# Revit family: RN 62010 Vanne à glissière
name_source: partatom
category: Rohrzubehör
units: mm (PartAtom-declared; Revit-internal decimal feet)

## family parameters
Arbeitsebenenbasiert = Nein
Beim Laden mit Abzugskörper schneiden = Nein
Bemaßung runder Anschluss = Durchmesser verwenden
Gemeinsam genutzt = Nein
Immer vertikal = Ja
Teiletyp = Ventil - Zerlegung in

## types (10) — shared parameters
1.010.00.2 Blattnummer der Richtlinie = 17
1.010.00.3 Ausgabedatum (Monat) der Richtlinie = 201601
1.010.00.4 Herstellername = R. Nussbaum AG
1.010.00.5 Revisionsdatum der Datei = 20190528
1.010.00.6 Webadresse des Herstellers = http://www.nussbaum.ch
1.100.00.3 Sortiernummer für Anzeigereihenfolge = 1
1.100.00.4 Produktbezeichnung = Absperrarmaturen
1.960/3L.00.8 Link (URL) = https://www.nussbaum.ch
17.700.00.4 Armaturentyp = 1
17.700.00.7 Maximale Betriebstemperatur TB [°C] = 40
17.700.00.8 Maximaler Betriebsdruck (Arbeitsdruck) ps [1.0 · 105 Pa] = 16
Connector Visibility = Nein
EnclosingSpace Visibility = Nein
Hersteller = R. Nussbauzm AG
URL = https://www.nussbaum.ch

## per-type parameters (varying)
- DN 25: 1.800.00.3 TGA-Nummer=00102100000000000000000000000400600000000000000001???00000; 1.810.00.3 Hersteller-Bestellnummer=62010.23; 1.810.00.4 DATANORM-Nummer=62010.23; 1.810.00.5 StLB-Nummer=721.153; 1.810.00.6 GTIN-Nummer=7612945672926; 17.700.00.30 Produktbeschreibung=62010.23, Schieber, mit Flanschen, DN=25; 17.700.00.5 Nennweite DN=25; 17.700.00.6 kvs-Wert [m3/h]=20.6; CONNECTOR0_DIAMETER_dX_0r=25 mm  [stored 0.082021 ft]; CONNECTOR0_dX_00=66 mm; CONNECTOR0_dX_01=65 mm; CONNECTOR0_ref_dX=66 mm; CONNECTOR1_DIAMETER_dX_0r=25 mm  [stored 0.082021 ft]; CONNECTOR1_dX_00=65 mm; CONNECTOR1_dX_01=66 mm; CONNECTOR1_ref_dX=66 mm; Modell=62010.23; R. Nussbaum AG 62010.23 de Visibility=Ja; R. Nussbaum AG 62010.24 de Visibility=Nein; R. Nussbaum AG 62010.25 de Visibility=Nein; R. Nussbaum AG 62010.26 de Visibility=Nein; R. Nussbaum AG 62010.27 de Visibility=Nein; R. Nussbaum AG 62010.28 de Visibility=Nein; R. Nussbaum AG 62010.29 de Visibility=Nein; R. Nussbaum AG 62010.30 de Visibility=Nein; R. Nussbaum AG 62010.31 de Visibility=Nein; R. Nussbaum AG 62010.32 de Visibility=Nein; Typenkommentare=Vanne à glissièreDN 25
- DN 32: 1.800.00.3 TGA-Nummer=00102100000000000000000000000400600000000000000002???00000; 1.810.00.3 Hersteller-Bestellnummer=62010.24; 1.810.00.4 DATANORM-Nummer=62010.24; 1.810.00.5 StLB-Nummer=721.154; 1.810.00.6 GTIN-Nummer=7612945672933; 17.700.00.30 Produktbeschreibung=62010.24, Schieber, mit Flanschen, DN=32; 17.700.00.5 Nennweite DN=32; 17.700.00.6 kvs-Wert [m3/h]=36.8; CONNECTOR0_DIAMETER_dX_0r=32 mm; CONNECTOR0_dX_00=71 mm; CONNECTOR0_dX_01=70 mm; CONNECTOR0_ref_dX=71 mm; CONNECTOR1_DIAMETER_dX_0r=32 mm; CONNECTOR1_dX_00=70 mm; CONNECTOR1_dX_01=71 mm; CONNECTOR1_ref_dX=71 mm; Modell=62010.24; R. Nussbaum AG 62010.23 de Visibility=Nein; R. Nussbaum AG 62010.24 de Visibility=Ja; R. Nussbaum AG 62010.25 de Visibility=Nein; R. Nussbaum AG 62010.26 de Visibility=Nein; R. Nussbaum AG 62010.27 de Visibility=Nein; R. Nussbaum AG 62010.28 de Visibility=Nein; R. Nussbaum AG 62010.29 de Visibility=Nein; R. Nussbaum AG 62010.30 de Visibility=Nein; R. Nussbaum AG 62010.31 de Visibility=Nein; R. Nussbaum AG 62010.32 de Visibility=Nein; Typenkommentare=Vanne à glissièreDN 32
- DN 40: 1.800.00.3 TGA-Nummer=00102100000000000000000000000400600000000000000003???00000; 1.810.00.3 Hersteller-Bestellnummer=62010.25; 1.810.00.4 DATANORM-Nummer=62010.25; 1.810.00.5 StLB-Nummer=721.155; 1.810.00.6 GTIN-Nummer=7612945016492; 17.700.00.30 Produktbeschreibung=62010.25, Schieber, mit Flanschen, DN=40; 17.700.00.5 Nennweite DN=40; 17.700.00.6 kvs-Wert [m3/h]=45.2; CONNECTOR0_DIAMETER_dX_0r=40 mm; CONNECTOR0_dX_00=71 mm; CONNECTOR0_dX_01=70 mm; CONNECTOR0_ref_dX=71 mm; CONNECTOR1_DIAMETER_dX_0r=40 mm; CONNECTOR1_dX_00=70 mm; CONNECTOR1_dX_01=71 mm; CONNECTOR1_ref_dX=71 mm; Modell=62010.25; R. Nussbaum AG 62010.23 de Visibility=Nein; R. Nussbaum AG 62010.24 de Visibility=Nein; R. Nussbaum AG 62010.25 de Visibility=Ja; R. Nussbaum AG 62010.26 de Visibility=Nein; R. Nussbaum AG 62010.27 de Visibility=Nein; R. Nussbaum AG 62010.28 de Visibility=Nein; R. Nussbaum AG 62010.29 de Visibility=Nein; R. Nussbaum AG 62010.30 de Visibility=Nein; R. Nussbaum AG 62010.31 de Visibility=Nein; R. Nussbaum AG 62010.32 de Visibility=Nein; Typenkommentare=Vanne à glissièreDN 40
- DN 50: 1.800.00.3 TGA-Nummer=00102100000000000000000000000400600000000000000004???00000; 1.810.00.3 Hersteller-Bestellnummer=62010.26; 1.810.00.4 DATANORM-Nummer=62010.26; 1.810.00.5 StLB-Nummer=721.156; 1.810.00.6 GTIN-Nummer=7612945016508; 17.700.00.30 Produktbeschreibung=62010.26, Schieber, mit Flanschen, DN=50; 17.700.00.5 Nennweite DN=50; 17.700.00.6 kvs-Wert [m3/h]=76.1; CONNECTOR0_DIAMETER_dX_0r=50 mm  [stored 0.164042 ft]; CONNECTOR0_dX_00=76 mm; CONNECTOR0_dX_01=75 mm; CONNECTOR0_ref_dX=76 mm; CONNECTOR1_DIAMETER_dX_0r=50 mm  [stored 0.164042 ft]; CONNECTOR1_dX_00=75 mm; CONNECTOR1_dX_01=76 mm; CONNECTOR1_ref_dX=76 mm; Modell=62010.26; R. Nussbaum AG 62010.23 de Visibility=Nein; R. Nussbaum AG 62010.24 de Visibility=Nein; R. Nussbaum AG 62010.25 de Visibility=Nein; R. Nussbaum AG 62010.26 de Visibility=Ja; R. Nussbaum AG 62010.27 de Visibility=Nein; R. Nussbaum AG 62010.28 de Visibility=Nein; R. Nussbaum AG 62010.29 de Visibility=Nein; R. Nussbaum AG 62010.30 de Visibility=Nein; R. Nussbaum AG 62010.31 de Visibility=Nein; R. Nussbaum AG 62010.32 de Visibility=Nein; Typenkommentare=Vanne à glissièreDN 50
- DN 65: 1.800.00.3 TGA-Nummer=00102100000000000000000000000400600000000000000005???00000; 1.810.00.3 Hersteller-Bestellnummer=62010.27; 1.810.00.4 DATANORM-Nummer=62010.27; 1.810.00.5 StLB-Nummer=721.157; 1.810.00.6 GTIN-Nummer=7612945016515; 17.700.00.30 Produktbeschreibung=62010.27, Schieber, mit Flanschen, DN=65; 17.700.00.5 Nennweite DN=65; 17.700.00.6 kvs-Wert [m3/h]=115.5; CONNECTOR0_DIAMETER_dX_0r=65 mm; CONNECTOR0_dX_00=86 mm; CONNECTOR0_dX_01=85 mm; CONNECTOR0_ref_dX=86 mm; CONNECTOR1_DIAMETER_dX_0r=65 mm; CONNECTOR1_dX_00=85 mm; CONNECTOR1_dX_01=86 mm; CONNECTOR1_ref_dX=86 mm; Modell=62010.27; R. Nussbaum AG 62010.23 de Visibility=Nein; R. Nussbaum AG 62010.24 de Visibility=Nein; R. Nussbaum AG 62010.25 de Visibility=Nein; R. Nussbaum AG 62010.26 de Visibility=Nein; R. Nussbaum AG 62010.27 de Visibility=Ja; R. Nussbaum AG 62010.28 de Visibility=Nein; R. Nussbaum AG 62010.29 de Visibility=Nein; R. Nussbaum AG 62010.30 de Visibility=Nein; R. Nussbaum AG 62010.31 de Visibility=Nein; R. Nussbaum AG 62010.32 de Visibility=Nein; Typenkommentare=Vanne à glissièreDN 65
- DN 80: 1.800.00.3 TGA-Nummer=00102100000000000000000000000400600000000000000006???00000; 1.810.00.3 Hersteller-Bestellnummer=62010.28; 1.810.00.4 DATANORM-Nummer=62010.28; 1.810.00.5 StLB-Nummer=721.158; 1.810.00.6 GTIN-Nummer=7612945016522; 17.700.00.30 Produktbeschreibung=62010.28, Schieber, mit Flanschen, DN=80; 17.700.00.5 Nennweite DN=80; 17.700.00.6 kvs-Wert [m3/h]=158.4; CONNECTOR0_DIAMETER_dX_0r=80 mm; CONNECTOR0_dX_00=91 mm; CONNECTOR0_dX_01=90 mm; CONNECTOR0_ref_dX=91 mm; CONNECTOR1_DIAMETER_dX_0r=80 mm; CONNECTOR1_dX_00=90 mm; CONNECTOR1_dX_01=91 mm; CONNECTOR1_ref_dX=91 mm; Modell=62010.28; R. Nussbaum AG 62010.23 de Visibility=Nein; R. Nussbaum AG 62010.24 de Visibility=Nein; R. Nussbaum AG 62010.25 de Visibility=Nein; R. Nussbaum AG 62010.26 de Visibility=Nein; R. Nussbaum AG 62010.27 de Visibility=Nein; R. Nussbaum AG 62010.28 de Visibility=Ja; R. Nussbaum AG 62010.29 de Visibility=Nein; R. Nussbaum AG 62010.30 de Visibility=Nein; R. Nussbaum AG 62010.31 de Visibility=Nein; R. Nussbaum AG 62010.32 de Visibility=Nein; Typenkommentare=Vanne à glissièreDN 80
- DN 100: 1.800.00.3 TGA-Nummer=00102100000000000000000000000400600000000000000007???00000; 1.810.00.3 Hersteller-Bestellnummer=62010.29; 1.810.00.4 DATANORM-Nummer=62010.29; 1.810.00.5 StLB-Nummer=721.161; 1.810.00.6 GTIN-Nummer=7612945016539; 17.700.00.30 Produktbeschreibung=62010.29, Schieber, mit Flanschen, DN=100; 17.700.00.5 Nennweite DN=100; 17.700.00.6 kvs-Wert [m3/h]=233; CONNECTOR0_DIAMETER_dX_0r=100 mm  [stored 0.328084 ft]; CONNECTOR0_dX_00=96 mm; CONNECTOR0_dX_01=95 mm; CONNECTOR0_ref_dX=96 mm; CONNECTOR1_DIAMETER_dX_0r=100 mm  [stored 0.328084 ft]; CONNECTOR1_dX_00=95 mm; CONNECTOR1_dX_01=96 mm; CONNECTOR1_ref_dX=96 mm; Modell=62010.29; R. Nussbaum AG 62010.23 de Visibility=Nein; R. Nussbaum AG 62010.24 de Visibility=Nein; R. Nussbaum AG 62010.25 de Visibility=Nein; R. Nussbaum AG 62010.26 de Visibility=Nein; R. Nussbaum AG 62010.27 de Visibility=Nein; R. Nussbaum AG 62010.28 de Visibility=Nein; R. Nussbaum AG 62010.29 de Visibility=Ja; R. Nussbaum AG 62010.30 de Visibility=Nein; R. Nussbaum AG 62010.31 de Visibility=Nein; R. Nussbaum AG 62010.32 de Visibility=Nein; Typenkommentare=Vanne à glissièreDN 100
- DN 125: 1.800.00.3 TGA-Nummer=0010210000000000000000000000040060000000000000000800000000; 1.810.00.3 Hersteller-Bestellnummer=62010.3; 1.810.00.4 DATANORM-Nummer=62010.3; 1.810.00.5 StLB-Nummer=721.162; 1.810.00.6 GTIN-Nummer=7612945016546; 17.700.00.30 Produktbeschreibung=62010.30, Schieber, mit Flanschen, DN=125; 17.700.00.5 Nennweite DN=125; 17.700.00.6 kvs-Wert [m3/h]=364; CONNECTOR0_DIAMETER_dX_0r=125 mm; CONNECTOR0_dX_00=101 mm; CONNECTOR0_dX_01=100 mm  [stored 0.328084 ft]; CONNECTOR0_ref_dX=101 mm; CONNECTOR1_DIAMETER_dX_0r=125 mm; CONNECTOR1_dX_00=100 mm  [stored 0.328084 ft]; CONNECTOR1_dX_01=101 mm; CONNECTOR1_ref_dX=101 mm; Modell=62010.3; R. Nussbaum AG 62010.23 de Visibility=Nein; R. Nussbaum AG 62010.24 de Visibility=Nein; R. Nussbaum AG 62010.25 de Visibility=Nein; R. Nussbaum AG 62010.26 de Visibility=Nein; R. Nussbaum AG 62010.27 de Visibility=Nein; R. Nussbaum AG 62010.28 de Visibility=Nein; R. Nussbaum AG 62010.29 de Visibility=Nein; R. Nussbaum AG 62010.30 de Visibility=Ja; R. Nussbaum AG 62010.31 de Visibility=Nein; R. Nussbaum AG 62010.32 de Visibility=Nein; Typenkommentare=Vanne à glissièreDN 125
- DN 150: 1.800.00.3 TGA-Nummer=0010210000000000000000000000040060000000000000000900000000; 1.810.00.3 Hersteller-Bestellnummer=62010.31; 1.810.00.4 DATANORM-Nummer=62010.31; 1.810.00.5 StLB-Nummer=721.163; 1.810.00.6 GTIN-Nummer=7612945728586; 17.700.00.30 Produktbeschreibung=62010.31, Schieber, mit Flanschen, DN=150; 17.700.00.5 Nennweite DN=150; 17.700.00.6 kvs-Wert [m3/h]=1600; CONNECTOR0_DIAMETER_dX_0r=150 mm; CONNECTOR0_dX_00=106 mm; CONNECTOR0_dX_01=105 mm; CONNECTOR0_ref_dX=106 mm; CONNECTOR1_DIAMETER_dX_0r=150 mm; CONNECTOR1_dX_00=105 mm; CONNECTOR1_dX_01=106 mm; CONNECTOR1_ref_dX=106 mm; Modell=62010.31; R. Nussbaum AG 62010.23 de Visibility=Nein; R. Nussbaum AG 62010.24 de Visibility=Nein; R. Nussbaum AG 62010.25 de Visibility=Nein; R. Nussbaum AG 62010.26 de Visibility=Nein; R. Nussbaum AG 62010.27 de Visibility=Nein; R. Nussbaum AG 62010.28 de Visibility=Nein; R. Nussbaum AG 62010.29 de Visibility=Nein; R. Nussbaum AG 62010.30 de Visibility=Nein; R. Nussbaum AG 62010.31 de Visibility=Ja; R. Nussbaum AG 62010.32 de Visibility=Nein; Typenkommentare=Vanne à glissièreDN 150
- DN 200: 1.800.00.3 TGA-Nummer=0010210000000000000000000000040060000000000000001000000000; 1.810.00.3 Hersteller-Bestellnummer=62010.32; 1.810.00.4 DATANORM-Nummer=62010.32; 1.810.00.5 StLB-Nummer=721.164; 1.810.00.6 GTIN-Nummer=7612945728593; 17.700.00.30 Produktbeschreibung=62010.32, Schieber, mit Flanschen, DN=200; 17.700.00.5 Nennweite DN=200; 17.700.00.6 kvs-Wert [m3/h]=3200; CONNECTOR0_DIAMETER_dX_0r=200 mm; CONNECTOR0_dX_00=116 mm; CONNECTOR0_dX_01=115 mm; CONNECTOR0_ref_dX=116 mm; CONNECTOR1_DIAMETER_dX_0r=200 mm; CONNECTOR1_dX_00=115 mm; CONNECTOR1_dX_01=116 mm; CONNECTOR1_ref_dX=116 mm; Modell=62010.32; R. Nussbaum AG 62010.23 de Visibility=Nein; R. Nussbaum AG 62010.24 de Visibility=Nein; R. Nussbaum AG 62010.25 de Visibility=Nein; R. Nussbaum AG 62010.26 de Visibility=Nein; R. Nussbaum AG 62010.27 de Visibility=Nein; R. Nussbaum AG 62010.28 de Visibility=Nein; R. Nussbaum AG 62010.29 de Visibility=Nein; R. Nussbaum AG 62010.30 de Visibility=Nein; R. Nussbaum AG 62010.31 de Visibility=Nein; R. Nussbaum AG 62010.32 de Visibility=Ja; Typenkommentare=Vanne à glissièreDN 200

note: [stored X ft] marks values corroborated as IEEE doubles in the binary element streams (Revit-internal decimal feet)

## geometry (parser evidence)
native form markers: Sweep x1
no freeform markers — native parametric forms only
